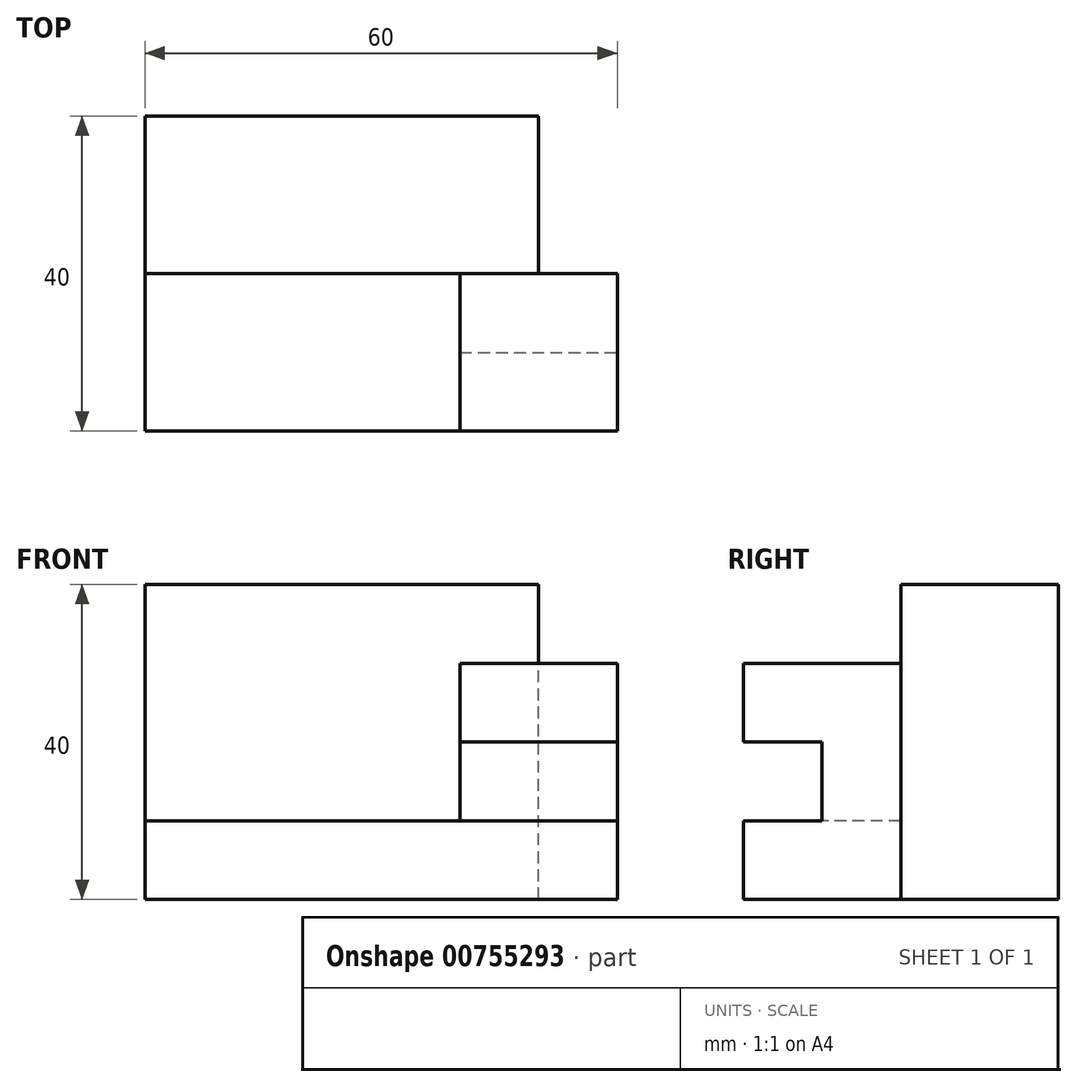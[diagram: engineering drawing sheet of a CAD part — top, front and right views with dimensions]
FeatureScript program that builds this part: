
annotation { "Feature Type Name" : "Feature", "Feature Type Description" : "" }
export const myFeature = defineFeature(function(context is Context, id is Id, definition is map)
    precondition{}
    {
        {
            var Q0;
            Q0=qCreatedBy(makeId("Front.planeOp"),FACE);
            var sketch = newSketch(context, id + "F0", { "sketchPlane" : qUnion([Q0])});
            skLineSegment(sketch, "E0", {"start": v(0, 0) * mm, "end": v(60, 0) * mm});
            skLineSegment(sketch, "E1", {"start": v(60, 0) * mm, "end": v(60, 40) * mm});
            skLineSegment(sketch, "E2", {"start": v(60, 40) * mm, "end": v(0, 40) * mm});
            skLineSegment(sketch, "E3", {"start": v(0, 40) * mm, "end": v(0, 0) * mm});
            skSolve(sketch);
        }
        {
            var Q0;
            Q0=makeQuery(id+"F0.imprint","IMPRINT",FACE,{"disambiguationData":[TD([[makeQuery(id+"F0.imprint","IMPRINT",EDGE,{"derivedFrom":sQuery(id+"F0.wireOp",EDGE,"E0")}),1.0]])]});
            extrude(context, id + "F1", {"entities" : qUnion([Q0]), "depth" : 40 * mm, "offsetDistance" : 25 * mm});
        }
        {
            var Q0;
            Q0=makeQuery(id+"F1.opExtrude","SWEPT_FACE",FACE,{"disambiguationData":[OSD([sQuery(id+"F0.wireOp",EDGE,"E2")])]});
            var sketch = newSketch(context, id + "F2", { "sketchPlane" : qUnion([Q0])});
            skLineSegment(sketch, "E4", {"start": v(60, 0) * mm, "end": v(50, 0) * mm});
            skLineSegment(sketch, "E5", {"start": v(50, 0) * mm, "end": v(50, -20) * mm});
            skLineSegment(sketch, "E6", {"start": v(50, -20) * mm, "end": v(60, -20) * mm});
            skLineSegment(sketch, "E7", {"start": v(60, -20) * mm, "end": v(60, 0) * mm});
            skSolve(sketch);
        }
        {
            var Q0;
            Q0=makeQuery(id+"F2.imprint","IMPRINT",FACE,{"disambiguationData":[TD([[makeQuery(id+"F2.imprint","IMPRINT",EDGE,{"derivedFrom":sQuery(id+"F2.wireOp",EDGE,"E4")}),1.0]])]});
            extrude(context, id + "F3", {"entities" : qUnion([Q0]), "operationType" : NewBodyOperationType.REMOVE, "oppositeDirection" : true, "depth" : 40 * mm, "offsetDistance" : 25 * mm});
        }
        {
            var Q0;
            Q0=makeQuery(id+"F1.opExtrude","SWEPT_FACE",FACE,{"disambiguationData":[OSD([sQuery(id+"F0.wireOp",EDGE,"E2")])]});
            var sketch = newSketch(context, id + "F4", { "sketchPlane" : qUnion([Q0])});
            skLineSegment(sketch, "E8", {"start": v(0, -40) * mm, "end": v(0, -20) * mm});
            skLineSegment(sketch, "E9", {"start": v(0, -20) * mm, "end": v(40, -20) * mm});
            skLineSegment(sketch, "E10", {"start": v(40, -20) * mm, "end": v(40, -40) * mm});
            skLineSegment(sketch, "E11", {"start": v(40, -40) * mm, "end": v(0, -40) * mm});
            skSolve(sketch);
        }
        {
            var Q0;
            Q0=makeQuery(id+"F4.imprint","IMPRINT",FACE,{"disambiguationData":[TD([[makeQuery(id+"F4.imprint","IMPRINT",EDGE,{"derivedFrom":sQuery(id+"F4.wireOp",EDGE,"E8")}),-1.0]])]});
            extrude(context, id + "F5", {"entities" : qUnion([Q0]), "operationType" : NewBodyOperationType.REMOVE, "oppositeDirection" : true, "depth" : 30 * mm, "offsetDistance" : 25 * mm});
        }
        {
            var Q0;
            Q0=makeQuery(id+"F1.opExtrude","SWEPT_FACE",FACE,{"disambiguationData":[OSD([sQuery(id+"F0.wireOp",EDGE,"E2")])]});
            var sketch = newSketch(context, id + "F6", { "sketchPlane" : qUnion([Q0])});
            skLineSegment(sketch, "E12", {"start": v(40, -40) * mm, "end": v(60, -40) * mm});
            skLineSegment(sketch, "E13", {"start": v(60, -40) * mm, "end": v(60, -20) * mm});
            skLineSegment(sketch, "E14", {"start": v(60, -20) * mm, "end": v(40, -20) * mm});
            skLineSegment(sketch, "E15", {"start": v(40, -20) * mm, "end": v(40, -40) * mm});
            skSolve(sketch);
        }
        {
            var Q0;
            Q0=makeQuery(id+"F6.imprint","IMPRINT",FACE,{"disambiguationData":[TD([[makeQuery(id+"F6.imprint","IMPRINT",EDGE,{"derivedFrom":sQuery(id+"F6.wireOp",EDGE,"E12")}),-1.0]])]});
            extrude(context, id + "F7", {"entities" : qUnion([Q0]), "operationType" : NewBodyOperationType.REMOVE, "oppositeDirection" : true, "depth" : 10 * mm, "offsetDistance" : 25 * mm});
        }
        {
            var Q0;
            Q0=makeQuery(id+"F1.opExtrude","SWEPT_FACE",FACE,{"disambiguationData":[OSD([sQuery(id+"F0.wireOp",EDGE,"E1")])]});
            var sketch = newSketch(context, id + "F8", { "sketchPlane" : qUnion([Q0])});
            skLineSegment(sketch, "E16", {"start": v(-40, 30) * mm, "end": v(-40, 20) * mm});
            skLineSegment(sketch, "E17", {"start": v(-40, 20) * mm, "end": v(-30, 20) * mm});
            skLineSegment(sketch, "E18", {"start": v(-30, 20) * mm, "end": v(-30, 10) * mm});
            skLineSegment(sketch, "E19", {"start": v(-30, 10) * mm, "end": v(-40, 10) * mm});
            skLineSegment(sketch, "E20", {"start": v(-40, 10) * mm, "end": v(-40, 20) * mm});
            skSolve(sketch);
        }
        {
            var Q0;
            Q0=makeQuery(id+"F8.imprint","IMPRINT",FACE,{"disambiguationData":[TD([[makeQuery(id+"F8.imprint","IMPRINT",EDGE,{"derivedFrom":sQuery(id+"F8.wireOp",EDGE,"E17")}),-1.0]])]});
            extrude(context, id + "F9", {"entities" : qUnion([Q0]), "operationType" : NewBodyOperationType.REMOVE, "oppositeDirection" : true, "depth" : 20 * mm, "offsetDistance" : 25 * mm});
        }
    });
